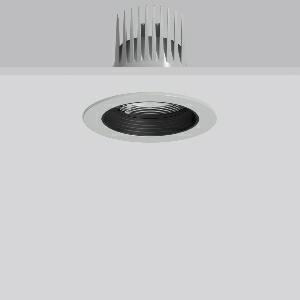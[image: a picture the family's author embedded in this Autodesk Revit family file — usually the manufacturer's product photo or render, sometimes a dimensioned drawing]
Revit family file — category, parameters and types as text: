
# Revit family: heledon_maxi_e_901767_004_3_76_575d
name_source: partatom
category: Lighting Fixtures
units: mm (PartAtom-declared; Revit-internal decimal feet)

## family parameters
Cut with Voids When Loaded = No
Host = Face
Light Source = No
Part Type = Normal
Room Calculation Point = No
Round Connector Dimension = Use Diameter
Shared = No

## types (1)
- HELEDON maxi E (1 x LED Modul 935, 3750 lm, 3500)
    Apparent Load = 35 VA
    Approval mark = CE
    CIE Flux Codes = 97 100 100 100 100
    Color Rendering = 92
    Color Temperature = 3500
    Default Elevation = 1800 mm
    Description = Series: HELEDON maxi
Round recessed downlight. Housing: die-cast aluminium, powder-coated. Black plastic ring and recessed LED to prevent glare from the side. Optical assembly with lens made of plastic (polycarbonate) for the best homogeneous light distribution - can be changed without tools. Best colour rendering index Ra>90. Suitable for Recessed ceiling mounting. Installation without tools thanks to spring fastening system. Including separate LED converter with connecting cable 600 mm.High quality converter without flickering and stroboscopic effect. Through-wiring box (5 pole) available as accessory. The following accessories can be mounted without use of tools: interchangeable lenses, decorative glasses, honeycomb louvre, clear and frosted diffusers, white interchangeable plastic ring. 
Colour: silver
Diameter: 162 mm
Height: 3 mm
Cut-out diameter: 152 mm
Recess height: 200 mm
Luminaire: recess height: 135 mm
Lamp: LED
Socket: without socket
Colour temperature: 3500K
Colour rendering index (CRI): 92
System power: 35 W
Rated luminous flux: 3750 lm
Luminous efficiency: 107 lm/W
Control gear: Converter, dimmable, DALI
Protection class: II
Type of protection: IP 20
    Height = 0 mm  [stored 0 ft]
    Lamp = 1 x LED Modul 935
    Lamp Light Flux = 3750 lm
    Lamp count = 1
    Length = 162 mm
    Lifetime = 50000 h
    Luminous efficacy = 107 lm/W
    Manufacturer = RZB
    ModVariant = No
    Model = 901767.004.3.76
    Mounting Place = Ceiling
    Mounting Type = Recessed
    Number of Poles = 1
    OnlyDefault = Yes
    Power Factor = 1
    Product Name = HELEDON maxi E
    Product group = Recessed downlights
    ProductGroupID = 402
    Protection Class = Protection class II
    Protection Degree = IP 20
    RLX_Detail_Level = 1
    RLX_Emergency_Light_Flux = 0 lm
    RLX_Emergency_Type = 0
    RLX_Emergency_Type_DB = No
    RlxData = <blob elided: 120313 chars, md5=aef7c389>
    Socket = socket
    Standby Power = 0 W
    System Light Flux = 3750 lm
    System Power = 35 W
    Type Comments = Product without accessories
    Type Image = 901663.004.jpg
    URL = http://relux.com
    VarID = ---
    Voltage = 230 V
    Voltage Range = 220-240 V
    Weight = 0.00 kg
    Width = 0 mm  [stored 0 ft]

note: [stored X ft] marks values corroborated as IEEE doubles in the binary element streams (Revit-internal decimal feet)

## geometry (parser evidence)
native form markers: Blend x4, Sweep x10
no freeform markers — native parametric forms only
